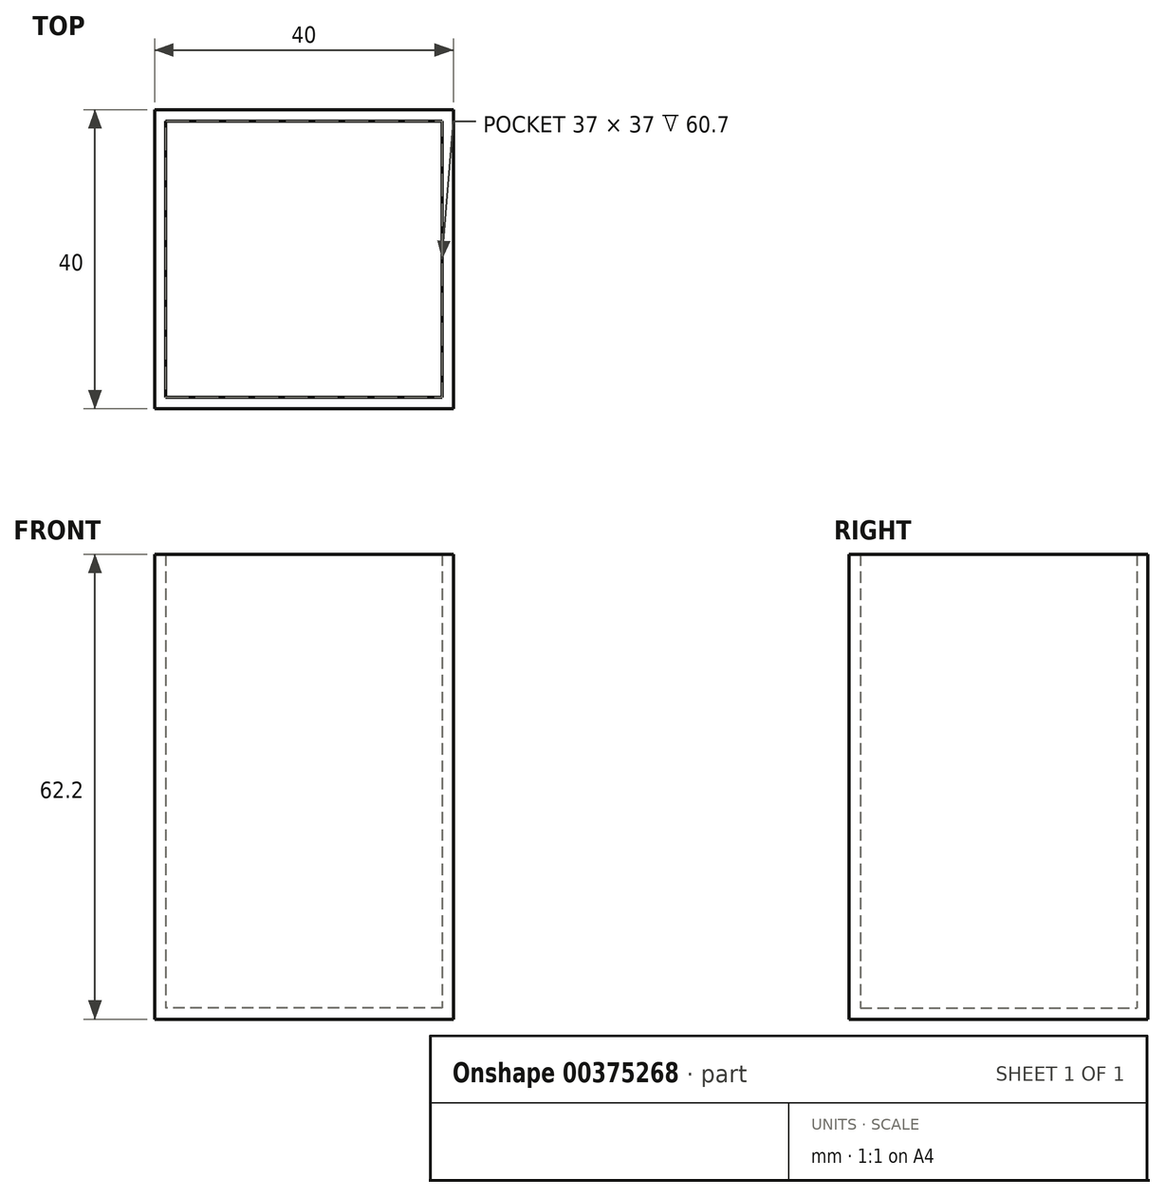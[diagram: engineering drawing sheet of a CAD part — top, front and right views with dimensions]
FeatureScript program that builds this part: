
annotation { "Feature Type Name" : "Feature", "Feature Type Description" : "" }
export const myFeature = defineFeature(function(context is Context, id is Id, definition is map)
    precondition{}
    {
        {
            var Q0;
            Q0=qCreatedBy(makeId("Top.planeOp"),FACE);
            var sketch = newSketch(context, id + "F0", { "sketchPlane" : qUnion([Q0])});
            skLineSegment(sketch, "E0", {"start": v(-21.34, 0) * mm, "end": v(-21.34, 20) * mm});
            skLineSegment(sketch, "E1", {"start": v(-21.34, 20) * mm, "end": v(18.66, 20) * mm});
            skLineSegment(sketch, "E2", {"start": v(18.66, 20) * mm, "end": v(18.66, -20) * mm});
            skLineSegment(sketch, "E3", {"start": v(18.66, -20) * mm, "end": v(-21.34, -20) * mm});
            skLineSegment(sketch, "E4", {"start": v(-21.34, -20) * mm, "end": v(-21.34, 0) * mm});
            skSolve(sketch);
        }
        {
            var Q0;
            Q0=makeQuery(id+"F0.imprint","IMPRINT",FACE,{"disambiguationData":[TD([[makeQuery(id+"F0.imprint","IMPRINT",EDGE,{"derivedFrom":sQuery(id+"F0.wireOp",EDGE,"E0")}),-1.0]])]});
            extrude(context, id + "F1", {"entities" : qUnion([Q0]), "depth" : 62.2 * mm});
        }
        {
            var Q0;
            Q0=makeQuery(id+"F1.opExtrude","CAP_FACE",FACE,{"disambiguationData":[OSD([sQuery(id+"F0.wireOp",EDGE,"E0"),sQuery(id+"F0.wireOp",EDGE,"E1"),sQuery(id+"F0.wireOp",EDGE,"E2"),sQuery(id+"F0.wireOp",EDGE,"E3"),sQuery(id+"F0.wireOp",EDGE,"E4")])],"isStart":false});
            shell(context, id + "F2", {"entities" : qUnion([Q0]), "thickness" : 1.5 * mm});
        }
    });
